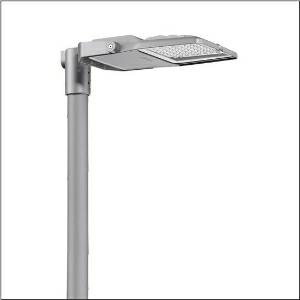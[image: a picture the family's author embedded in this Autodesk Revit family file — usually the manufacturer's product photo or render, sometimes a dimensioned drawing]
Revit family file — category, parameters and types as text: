
# Revit family: floodlight_fl_21_iq_mini___pl52_5xa7772b2d3a_55c6
name_source: partatom
category: Lighting Fixtures
units: mm (PartAtom-declared; Revit-internal decimal feet)

## family parameters
Cut with Voids When Loaded = No
Host = Face
Light Source = No
Part Type = Normal
Room Calculation Point = No
Round Connector Dimension = Use Diameter
Shared = No

## types (1)
- --- (1 x LED, 6240 lm, 45.5 W, 3000K)
    Apparent Load = 46 VA
    CIE Flux Codes = 26 60 98 100 100
    Color Rendering = 70
    Color Temperature = 3000K
    Default Elevation = 1800 mm
    Description = Floodlight FL 21 iQ mini, floodlight, primary light control with lens, of PMMA, primary optical cover: protective disc, of toughened safety glass, transparent, light distribution: PL52, light emission: direct distribution, installation type: surface-mounted, LED, High Power LED, rated luminous flux: 6.240lm, luminous efficacy: 137lm/W, light colour: 730, colour temperature: 3000K, control gear: iQ Street-Remote/DALI, control: Auto-Match, Temp-Guard, Night-Set, Smart-Wire, Desk-Remote (wireless, voltage-free reading and setting of iQ features in the workshop via application-optimized NFC function/RFID function), optimised constant luminous flux control (CLO 2.0), Light-Fading, Lumen-Switch, with terminal, 6-pole, mains connection: 220..240V, AC, 50/60Hz, start of lifetime: 46W, end of service life: 48W, reduction: 22W, luminaire housing, of diecast aluminium, powder-coated, Siteco® metallic grey (DB 702S), corrosivity category C5 mid according to DIN EN ISO 12944, suitable for swimming pools, chlorine-resistant, sealing non-destructively replaceable, please order mast flange separately, mast bracket, of steel, galvanised, powder-coated, protection rating (complete): IP66, insulation class (complete): insulation class II (safety insulation), certification: CE, ENEC, VDE, protection symbol: D, impact resistance: IK08, permissible operating ambient temperature: -40..+40°C, permissible operating ambient temperature for outdoor applications: -40..+50°C, standard: DIN EN 12944, LABS conformity tested according to VDMA 24364:2018-05, packaging unit: 1 piece

Light Distribution: PL52
    Height = 70 mm
    Lamp = 1 x LED
    Lamp Light Flux = 6240 lm
    Lamp Power = 45.5 W
    Lamp count = 1
    Length = 485 mm
    Luminous efficacy = 137 lm/W
    Manufacturer = Siteco
    ModVariant = No
    Model = 5XA7772B2D3A
    Number of Poles = 1
    OnlyDefault = Yes
    Power Factor = 1
    Product Name = Floodlight FL 21 iQ mini | PL52
    Product group = floodlight | pylon annexe
    ProductGroupID = 6201
    Protection Class = Protection class II
    Protection Degree = IP 66
    RLX_Detail_Level = 1
    RLX_Emergency_Light_Flux = 0 lm
    RLX_Emergency_Type = 0
    RLX_Emergency_Type_DB = No
    RlxData = <blob elided: 101421 chars, md5=9859015a>
    Socket = socket
    Standby Power = 0 W
    System Light Flux = 6240 lm
    System Power = 46 W
    Type Comments = factory setting: luminous flux: 100 % | dim-lin: 254 | 463 mA
    Type Image = l_1007125.jpg
    URL = http://relux.com
    VarID = @adj_186301
    Voltage = 0 V
    Weight = 0.00 kg
    Width = 337 mm

## geometry (parser evidence)
native form markers: Blend x4, Sweep x13
no freeform markers — native parametric forms only
